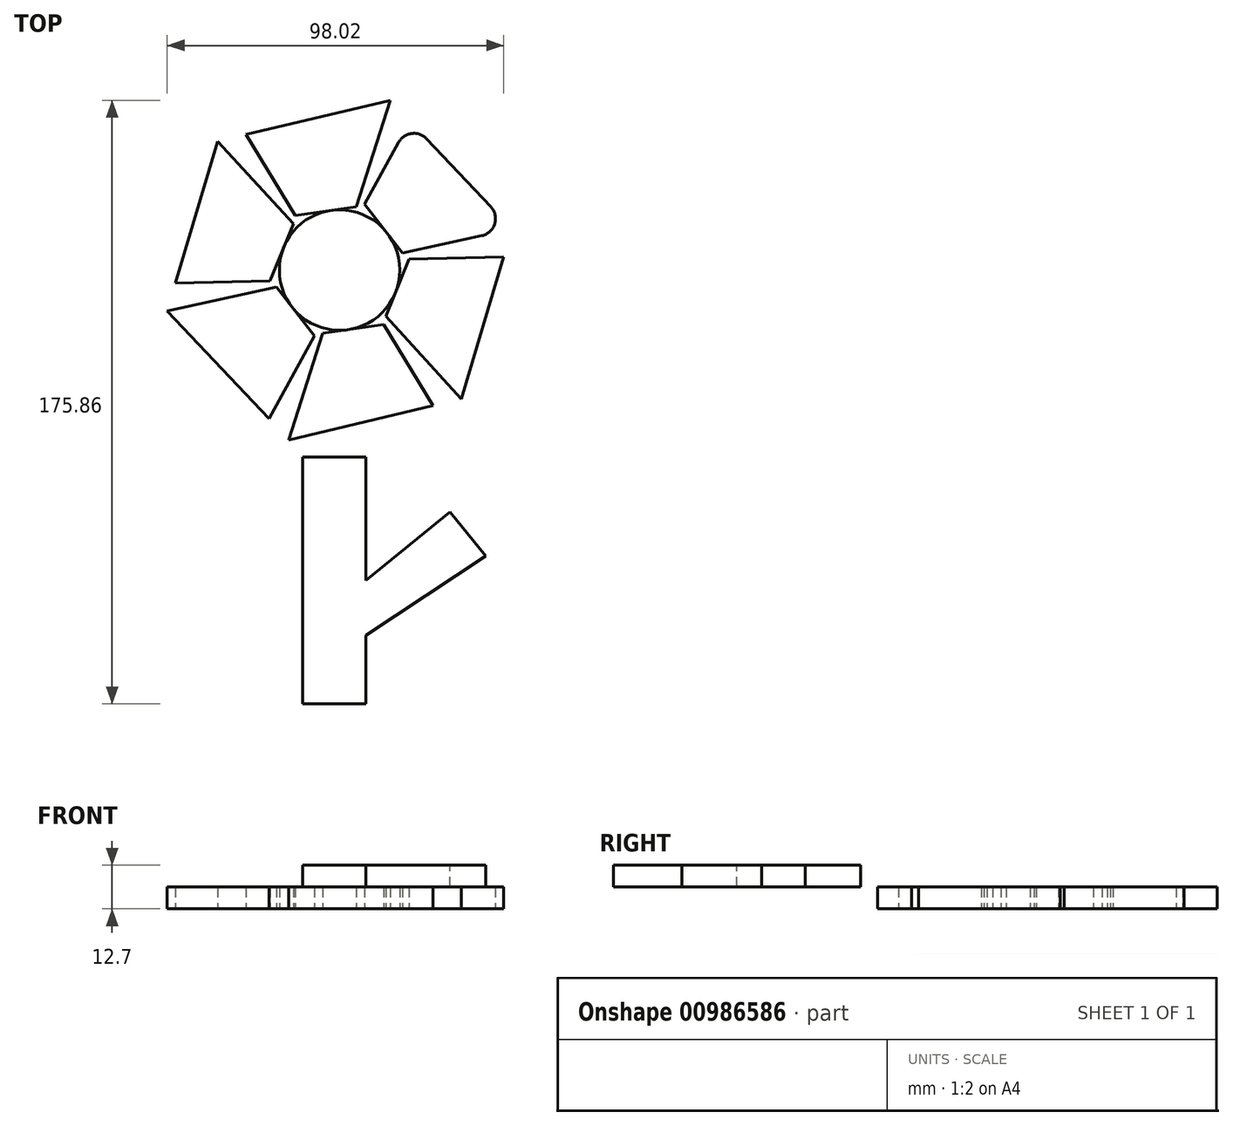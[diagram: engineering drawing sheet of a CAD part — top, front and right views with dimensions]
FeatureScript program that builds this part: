
annotation { "Feature Type Name" : "Feature", "Feature Type Description" : "" }
export const myFeature = defineFeature(function(context is Context, id is Id, definition is map)
    precondition{}
    {
        {
            var Q0;
            Q0=qCreatedBy(makeId("Top.planeOp"),FACE);
            var sketch = newSketch(context, id + "F0", { "sketchPlane" : qUnion([Q0])});
            skCircle(sketch, "E0", {"center": v(0, 0) * mm, "radius": 17.55 * mm});
            skLineSegment(sketch, "E1", {"start": v(7.34, 19.14) * mm, "end": v(18.38, 4.95) * mm});
            skLineSegment(sketch, "E2", {"start": v(18.38, 4.95) * mm, "end": v(50.22, 11.94) * mm});
            skLineSegment(sketch, "E3", {"start": v(50.22, 11.94) * mm, "end": v(20.58, 43.31) * mm});
            skLineSegment(sketch, "E4", {"start": v(20.58, 43.31) * mm, "end": v(7.34, 19.14) * mm});
            skLineSegment(sketch, "E5.1.0", {"start": v(-27.22, 39.48) * mm, "end": v(-12.9, 15.93) * mm});
            skLineSegment(sketch, "E5.1.1", {"start": v(14.77, 49.47) * mm, "end": v(-27.22, 39.48) * mm});
            skLineSegment(sketch, "E5.1.2", {"start": v(4.9, 18.4) * mm, "end": v(14.77, 49.47) * mm});
            skLineSegment(sketch, "E5.1.3", {"start": v(-12.9, 15.93) * mm, "end": v(4.9, 18.4) * mm});
            skLineSegment(sketch, "E5.2.0", {"start": v(-47.8, -3.84) * mm, "end": v(-20.24, -3.21) * mm});
            skLineSegment(sketch, "E5.2.1", {"start": v(-35.45, 37.52) * mm, "end": v(-47.8, -3.84) * mm});
            skLineSegment(sketch, "E5.2.2", {"start": v(-13.48, 13.44) * mm, "end": v(-35.45, 37.52) * mm});
            skLineSegment(sketch, "E5.2.3", {"start": v(-20.24, -3.21) * mm, "end": v(-13.48, 13.44) * mm});
            skLineSegment(sketch, "E5.3.0", {"start": v(-20.58, -43.31) * mm, "end": v(-7.34, -19.14) * mm});
            skLineSegment(sketch, "E5.3.1", {"start": v(-50.22, -11.94) * mm, "end": v(-20.58, -43.31) * mm});
            skLineSegment(sketch, "E5.3.2", {"start": v(-18.38, -4.95) * mm, "end": v(-50.22, -11.94) * mm});
            skLineSegment(sketch, "E5.3.3", {"start": v(-7.34, -19.14) * mm, "end": v(-18.38, -4.95) * mm});
            skLineSegment(sketch, "E5.4.0", {"start": v(27.22, -39.48) * mm, "end": v(12.9, -15.93) * mm});
            skLineSegment(sketch, "E5.4.1", {"start": v(-14.77, -49.47) * mm, "end": v(27.22, -39.48) * mm});
            skLineSegment(sketch, "E5.4.2", {"start": v(-4.9, -18.4) * mm, "end": v(-14.77, -49.47) * mm});
            skLineSegment(sketch, "E5.4.3", {"start": v(12.9, -15.93) * mm, "end": v(-4.9, -18.4) * mm});
            skLineSegment(sketch, "E5.5.0", {"start": v(47.8, 3.84) * mm, "end": v(20.24, 3.21) * mm});
            skLineSegment(sketch, "E5.5.1", {"start": v(35.45, -37.52) * mm, "end": v(47.8, 3.84) * mm});
            skLineSegment(sketch, "E5.5.2", {"start": v(13.48, -13.44) * mm, "end": v(35.45, -37.52) * mm});
            skLineSegment(sketch, "E5.5.3", {"start": v(20.24, 3.21) * mm, "end": v(13.48, -13.44) * mm});
            skSolve(sketch);
        }
        {
            var Q0;
            {var subQ1=sQuery(id+"F0.wireOp",EDGE,"E5.1.0");Q0=makeQuery(id+"F0.imprint","IMPRINT",FACE,{"disambiguationData":[TD([[makeQuery(id+"F0.imprint","IMPRINT",EDGE,{"derivedFrom":subQ1}),1.0]])]});}
            var Q1;
            {var subQ1=sQuery(id+"F0.wireOp",EDGE,"E5.2.0");Q1=makeQuery(id+"F0.imprint","IMPRINT",FACE,{"disambiguationData":[TD([[makeQuery(id+"F0.imprint","IMPRINT",EDGE,{"derivedFrom":subQ1}),1.0]])]});}
            var Q2;
            {var subQ0=sQuery(id+"F0.wireOp",EDGE,"E2");Q2=makeQuery(id+"F0.imprint","IMPRINT",FACE,{"disambiguationData":[TD([[makeQuery(id+"F0.imprint","IMPRINT",EDGE,{"derivedFrom":subQ0}),1.0]])]});}
            var Q3;
            {var subQ0=sQuery(id+"F0.wireOp",EDGE,"E0");var subQ4=makeQuery(id+"F0.imprint","INTERSECT",VERTEX,{"derivedFrom":[subQ0,sQuery(id+"F0.wireOp",EDGE,"E5.1.3")]});Q3=makeQuery(id+"F0.imprint","IMPRINT",FACE,{"disambiguationData":[TD([[makeQuery(id+"F0.imprint","IMPRINT",EDGE,{"disambiguationData":[TD([[subQ4,1.0]])],"derivedFrom":subQ0}),1.0]])]});}
            var Q4;
            {var subQ1=sQuery(id+"F0.wireOp",EDGE,"E5.5.0");Q4=makeQuery(id+"F0.imprint","IMPRINT",FACE,{"disambiguationData":[TD([[makeQuery(id+"F0.imprint","IMPRINT",EDGE,{"derivedFrom":subQ1}),1.0]])]});}
            var Q5;
            {var subQ1=sQuery(id+"F0.wireOp",EDGE,"E5.4.0");Q5=makeQuery(id+"F0.imprint","IMPRINT",FACE,{"disambiguationData":[TD([[makeQuery(id+"F0.imprint","IMPRINT",EDGE,{"derivedFrom":subQ1}),1.0]])]});}
            var Q6;
            {var subQ1=sQuery(id+"F0.wireOp",EDGE,"E5.3.0");Q6=makeQuery(id+"F0.imprint","IMPRINT",FACE,{"disambiguationData":[TD([[makeQuery(id+"F0.imprint","IMPRINT",EDGE,{"derivedFrom":subQ1}),1.0]])]});}
            extrude(context, id + "F1", {"entities" : qUnion([Q0, Q1, Q2, Q3, Q4, Q5, Q6]), "depth" : 6.35 * mm, "offsetDistance" : 25.4 * mm});
        }
        {
            var Q0;
            Q0=makeQuery(id+"F1.opExtrude","SWEPT_EDGE",EDGE,{"disambiguationData":[OSD([sQuery(id+"F0.wireOp",EDGE,"E2"),sQuery(id+"F0.wireOp",EDGE,"E3")])]});
            var Q1;
            Q1=makeQuery(id+"F1.opExtrude","SWEPT_EDGE",EDGE,{"disambiguationData":[OSD([sQuery(id+"F0.wireOp",EDGE,"E3"),sQuery(id+"F0.wireOp",EDGE,"E4")])]});
            fillet(context, id + "F2", {"entities" : qUnion([Q0, Q1]), "radius" : 5.08 * mm, "tangentPropagation" : true, "allowEdgeOverflow" : false});
        }
        {
            var Q0;
            Q0=makeQuery(id+"F1.opExtrude","CAP_FACE",FACE,{"disambiguationData":[OSD([sQuery(id+"F0.wireOp",EDGE,"E5.4.0"),sQuery(id+"F0.wireOp",EDGE,"E5.4.1"),sQuery(id+"F0.wireOp",EDGE,"E5.4.2"),sQuery(id+"F0.wireOp",EDGE,"E5.4.3")])],"isStart":false});
            var sketch = newSketch(context, id + "F3", { "sketchPlane" : qUnion([Q0])});
            skLineSegment(sketch, "E6.bottom", {"start": v(-10.72, -54.44) * mm, "end": v(7.7, -54.44) * mm});
            skLineSegment(sketch, "E6.top", {"start": v(-10.72, -126.39) * mm, "end": v(7.7, -126.39) * mm});
            skLineSegment(sketch, "E6.left", {"start": v(-10.72, -54.44) * mm, "end": v(-10.72, -126.39) * mm});
            skLineSegment(sketch, "E6.right", {"start": v(7.7, -54.44) * mm, "end": v(7.7, -126.39) * mm});
            skSolve(sketch);
        }
        {
            var Q0;
            Q0 = qSketchRegion(id + "F3", true);
            extrude(context, id + "F4", {"entities" : qUnion([Q0]), "depth" : 6.35 * mm, "offsetDistance" : 25.4 * mm});
        }
        {
            var Q0;
            Q0=makeQuery(id+"F4.opExtrude","CAP_FACE",FACE,{"disambiguationData":[OSD([sQuery(id+"F3.wireOp",EDGE,"E6.bottom"),sQuery(id+"F3.wireOp",EDGE,"E6.top"),sQuery(id+"F3.wireOp",EDGE,"E6.left"),sQuery(id+"F3.wireOp",EDGE,"E6.right")])],"isStart":false});
            var sketch = newSketch(context, id + "F5", { "sketchPlane" : qUnion([Q0])});
            skLineSegment(sketch, "E7", {"start": v(7.7, -90.41) * mm, "end": v(32.15, -70.45) * mm});
            skLineSegment(sketch, "E8", {"start": v(32.15, -70.45) * mm, "end": v(42.6, -83.25) * mm});
            skLineSegment(sketch, "E9", {"start": v(42.6, -83.25) * mm, "end": v(7.7, -106.45) * mm});
            skLineSegment(sketch, "E10", {"start": v(7.7, -106.45) * mm, "end": v(7.7, -90.41) * mm});
            skSolve(sketch);
        }
        {
            var Q0;
            Q0 = qSketchRegion(id + "F5", true);
            extrude(context, id + "F6", {"entities" : qUnion([Q0]), "operationType" : NewBodyOperationType.ADD, "oppositeDirection" : true, "depth" : 6.35 * mm, "offsetDistance" : 25.4 * mm});
        }
    });
